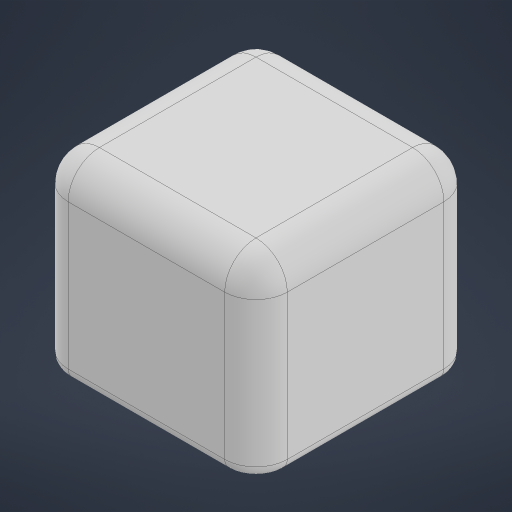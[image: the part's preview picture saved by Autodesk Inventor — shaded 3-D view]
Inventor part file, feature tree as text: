
AUTODESK INVENTOR PART (.ipt)
format: ipt  version: 2024.1 (Build 281209000, 209)  size: 582,144 bytes
history: native  units: mm
features: fillet x4, extrude x2, sketch x2
ambient origin geometry x8: Origin, YZ Plane, XZ Plane, XY Plane, X Axis, Y Axis, Z Axis, Center Point
bodies: Solid1 (feature_tree)
feature tree (8):
  extrude  "Extrusion1"  Depth=20.0mm
  extrude  "Extrusion2"  Depth=1.0mm TaperAngle=0.0deg
  fillet  "Fillet1"  Radius=4.0mm
  fillet  "Fillet2"  Radius=4.0mm
  fillet  "Fillet3"  Radius=1.5mm
  fillet  "Fillet4"  Radius=1.0mm
  sketch  "Sketch1"  dims[d0=20.0mm d1=4.0mm]
  sketch  "Sketch2"  dims[d2=20.0mm d3=0.0mm d4=4.0mm d5=0.0mm d6=4.0mm d7=4.0mm d8=1.5mm d9=1.0mm d10=1.0mm]
